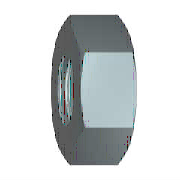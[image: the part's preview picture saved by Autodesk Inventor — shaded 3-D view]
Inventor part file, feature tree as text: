
AUTODESK INVENTOR PART (.ipt)
format: ipt  version: 2021 (Build 250183000, 183)  size: 173,056 bytes
history: native  units: mm (DEFAULTED — no unit token found)
features: sketch x3, chamfer x1, hole x1, other x1, plane x1
ambient origin geometry x7: Origin, YZ Plane, XZ Plane, X Axis, Y Axis, Z Axis, Center Point
bodies: Solid1 (feature_tree), Body (feature_tree)
feature tree (7):
  chamfer  "Chamfer1"  Angle=30.0deg  [1 undecoded]
  hole  "Thread"  [1 undecoded]
  other  "Work Axis1"
  plane  "Work Plane1"
  sketch  "Sketch1"  dims[d0=15.011107mm]
  sketch  "Sketch2"  dims[d1=6.8mm]
  sketch  "Sketch3"  dims[d2=0.0mm d3=30.0deg d4=30.0deg d5=13.0mm d6=13.0mm d7=90.0deg d25=6.647mm d26=6.0mm d27=4.0mm d28=2.0mm d29=14.3117mm d30=8.0mm d31=20.594885mm d8=0.676582mm d9=30.0deg d10=0.676582mm d11=30.0deg d13=0.0mm d14=0.0mm d39=0.0mm d40=0.676582mm d41=0.676582mm d42=0.0mm]
note: 2 required parameter values undecoded (feature->parameter linkage not recoverable at this tier; creation-order binding heuristic only, values carry confidence <= 0.55)
